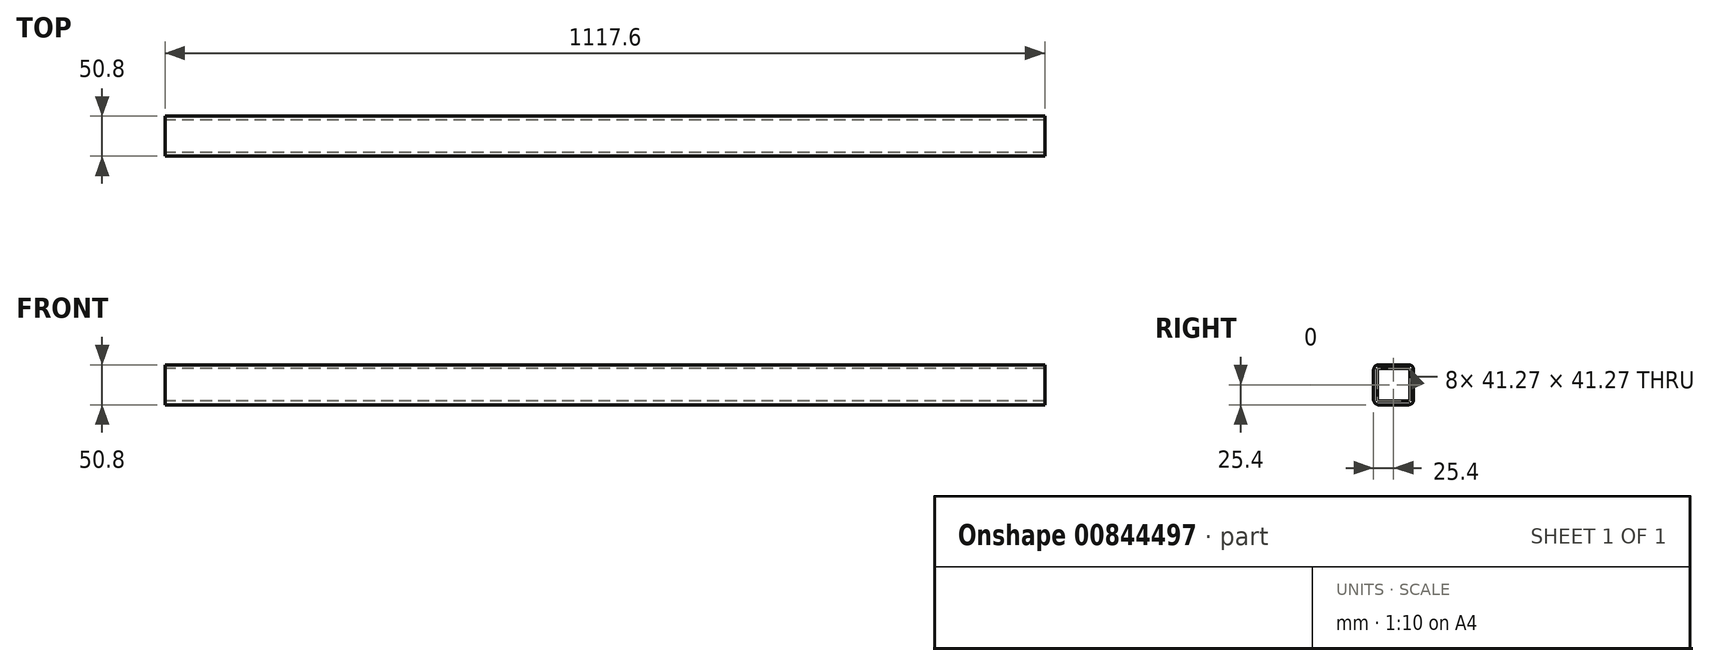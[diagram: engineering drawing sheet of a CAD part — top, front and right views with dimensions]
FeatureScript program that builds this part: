
annotation { "Feature Type Name" : "Feature", "Feature Type Description" : "" }
export const myFeature = defineFeature(function(context is Context, id is Id, definition is map)
    precondition{}
    {
        {
            var Q0;
            Q0=qCreatedBy(makeId("Right.planeOp"),FACE);
            var sketch = newSketch(context, id + "F0", { "sketchPlane" : qUnion([Q0])});
            skLineSegment(sketch, "E0.bottom", {"start": v(19.05, -25.4) * mm, "end": v(-19.05, -25.4) * mm});
            skLineSegment(sketch, "E0.top", {"start": v(19.05, 25.4) * mm, "end": v(-19.05, 25.4) * mm});
            skLineSegment(sketch, "E0.left", {"start": v(25.4, -19.05) * mm, "end": v(25.4, 19.05) * mm});
            skLineSegment(sketch, "E0.right", {"start": v(-25.4, -19.05) * mm, "end": v(-25.4, 19.05) * mm});
            skPoint(sketch, "E0.middle", {"position": v(0, 0) * mm});
            skPoint(sketch, "E1.visualSharp", {"position": v(-25.4, 25.4) * mm});
            skArc(sketch, "E1.filletArc", {"start": v(-19.05, 25.4) * mm, "mid": v(-23.54, 23.54) * mm, "end": v(-25.4, 19.05) * mm});
            skPoint(sketch, "E2.visualSharp", {"position": v(25.4, 25.4) * mm});
            skArc(sketch, "E2.filletArc", {"start": v(25.4, 19.05) * mm, "mid": v(23.54, 23.54) * mm, "end": v(19.05, 25.4) * mm});
            skPoint(sketch, "E3.visualSharp", {"position": v(25.4, -25.4) * mm});
            skArc(sketch, "E3.filletArc", {"start": v(19.05, -25.4) * mm, "mid": v(23.54, -23.54) * mm, "end": v(25.4, -19.05) * mm});
            skPoint(sketch, "E4.visualSharp", {"position": v(-25.4, -25.4) * mm});
            skArc(sketch, "E4.filletArc", {"start": v(-25.4, -19.05) * mm, "mid": v(-23.54, -23.54) * mm, "end": v(-19.05, -25.4) * mm});
            skLineSegment(sketch, "E5.0", {"start": v(20.64, -20.64) * mm, "end": v(20.64, 20.64) * mm});
            skLineSegment(sketch, "E5.1", {"start": v(20.64, -20.64) * mm, "end": v(-20.64, -20.64) * mm});
            skLineSegment(sketch, "E5.2", {"start": v(-20.64, -20.64) * mm, "end": v(-20.64, 20.64) * mm});
            skLineSegment(sketch, "E5.3", {"start": v(20.64, 20.64) * mm, "end": v(-20.64, 20.64) * mm});
            skSolve(sketch);
        }
        {
            var Q0;
            Q0=makeQuery(id+"F0.imprint","IMPRINT",FACE,{"disambiguationData":[TD([[makeQuery(id+"F0.imprint","IMPRINT",EDGE,{"derivedFrom":sQuery(id+"F0.wireOp",EDGE,"E0.bottom")}),-1.0]])]});
            extrude(context, id + "F1", {"entities" : qUnion([Q0]), "depth" : 1117.6 * mm, "offsetDistance" : 25.4 * mm, "symmetric" : true});
        }
    });
